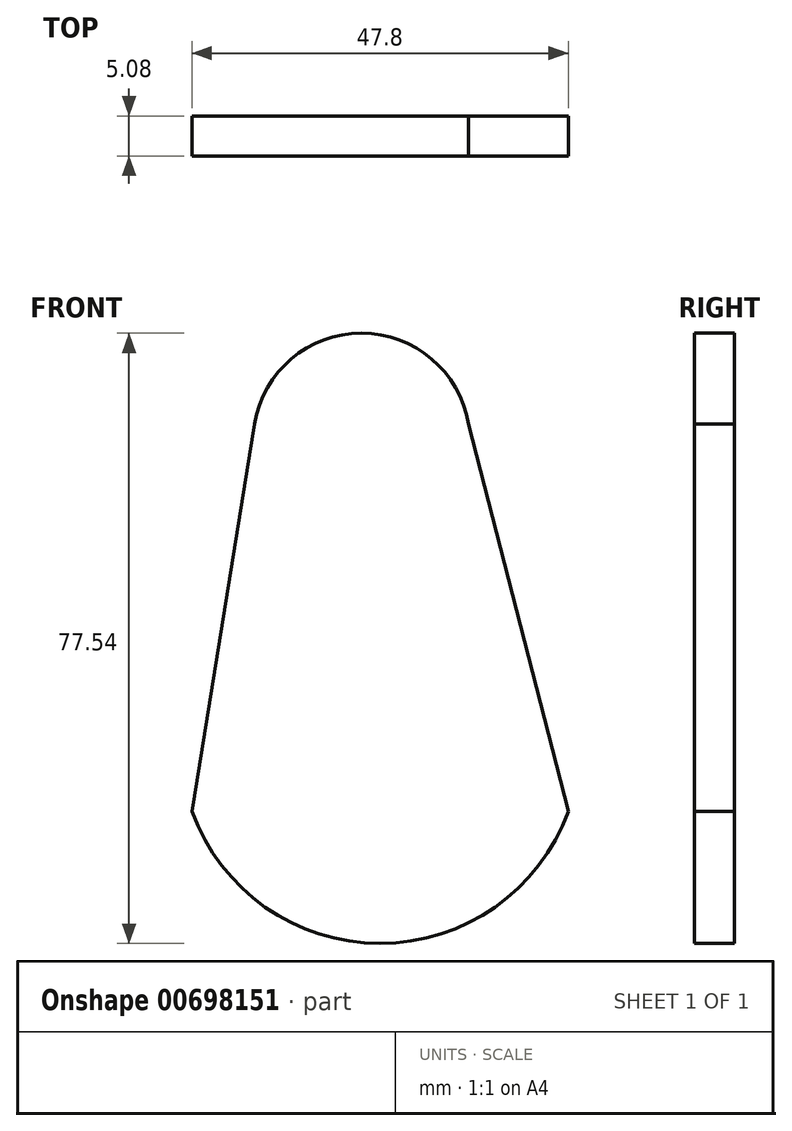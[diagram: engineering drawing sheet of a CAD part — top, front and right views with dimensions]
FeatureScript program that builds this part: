
annotation { "Feature Type Name" : "Feature", "Feature Type Description" : "" }
export const myFeature = defineFeature(function(context is Context, id is Id, definition is map)
    precondition{}
    {
        {
            var Q0;
            Q0=qCreatedBy(makeId("Front.planeOp"),FACE);
            var sketch = newSketch(context, id + "F0", { "sketchPlane" : qUnion([Q0])});
            skLineSegment(sketch, "E0", {"start": v(9.86, 6.77) * mm, "end": v(22.56, -42.42) * mm});
            skLineSegment(sketch, "E1", {"start": v(-17.3, 6.77) * mm, "end": v(-25.24, -42.42) * mm});
            skArc(sketch, "E2", {"start": v(9.86, 6.77) * mm, "mid": v(-3.72, 18.33) * mm, "end": v(-17.3, 6.77) * mm});
            skArc(sketch, "E3", {"start": v(-25.24, -42.42) * mm, "mid": v(-1.34, -59.21) * mm, "end": v(22.56, -42.42) * mm});
            skSolve(sketch);
        }
        {
            var Q0;
            Q0=qSketchRegion(id+"F0",true);
            extrude(context, id + "F1", {"entities" : qUnion([Q0]), "depth" : 5.08 * mm, "offsetDistance" : 25.4 * mm});
        }
    });
